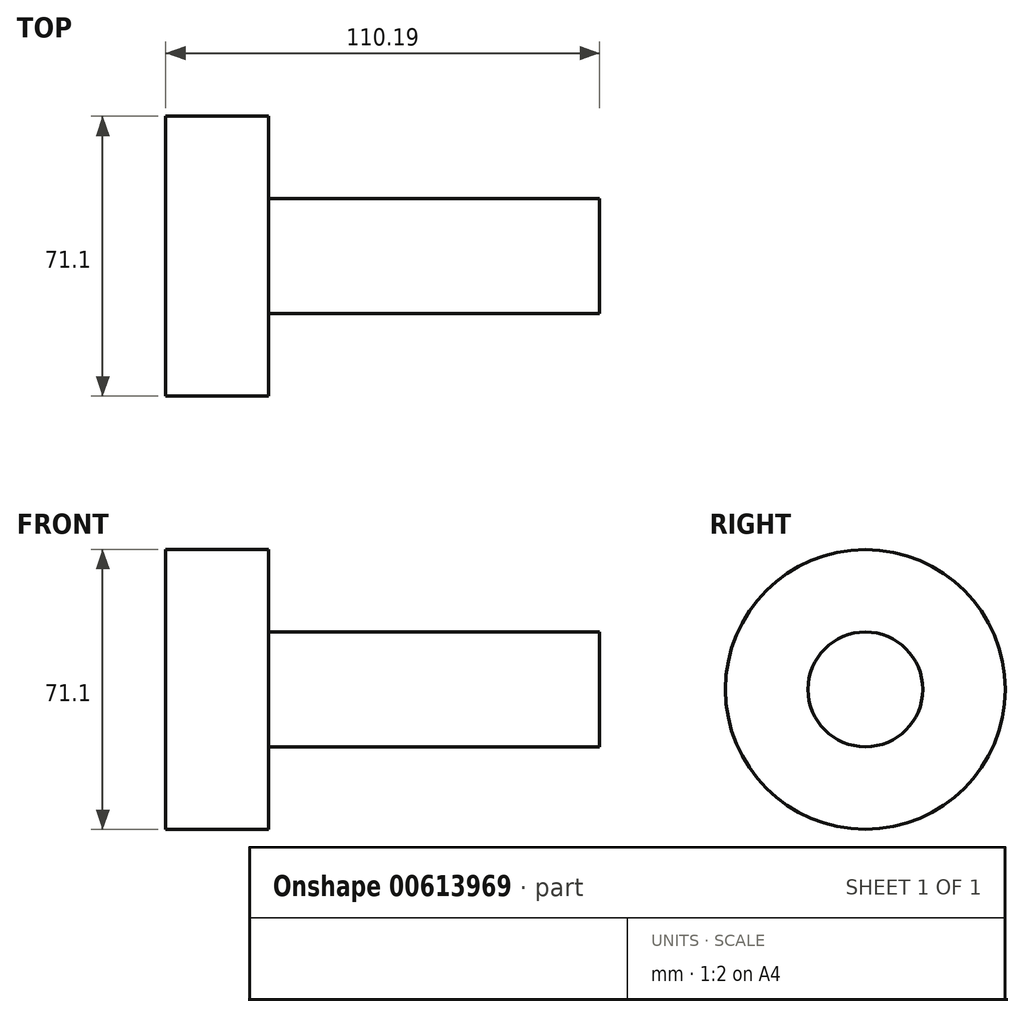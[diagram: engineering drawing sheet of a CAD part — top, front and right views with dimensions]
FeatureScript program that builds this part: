
annotation { "Feature Type Name" : "Feature", "Feature Type Description" : "" }
export const myFeature = defineFeature(function(context is Context, id is Id, definition is map)
    precondition{}
    {
        {
            var Q0;
            Q0=qCreatedBy(makeId("Top.planeOp"),FACE);
            var sketch = newSketch(context, id + "F0", { "sketchPlane" : qUnion([Q0])});
            skLineSegment(sketch, "E0", {"start": v(-60.48, 0) * mm, "end": v(49.71, 0) * mm});
            skLineSegment(sketch, "E1", {"start": v(49.71, 0) * mm, "end": v(49.71, 14.59) * mm});
            skPoint(sketch, "E2.end.orphan", {"position": v(0, 14.59) * mm});
            skLineSegment(sketch, "E3", {"start": v(49.71, 14.59) * mm, "end": v(-34.42, 14.59) * mm});
            skLineSegment(sketch, "E4", {"start": v(-34.42, 14.59) * mm, "end": v(-34.42, 35.55) * mm});
            skLineSegment(sketch, "E5", {"start": v(-34.42, 35.55) * mm, "end": v(-60.48, 35.55) * mm});
            skLineSegment(sketch, "E6", {"start": v(-60.48, 35.55) * mm, "end": v(-60.48, 0) * mm});
            skLineSegment(sketch, "E7", {"start": v(-34.42, 14.59) * mm, "end": v(-34.42, 0) * mm});
            skSolve(sketch);
        }
        {
            var Q0;
            Q0 = qSketchRegion(id + "F0", true);
            var Q1;
            Q1=sQuery(id+"F0.wireOp",EDGE,"E0");
            revolve(context, id + "F1", {"entities" : qUnion([Q0]), "axis" : qUnion([Q1]), "revolveType" : RevolveType.FULL});
        }
    });
